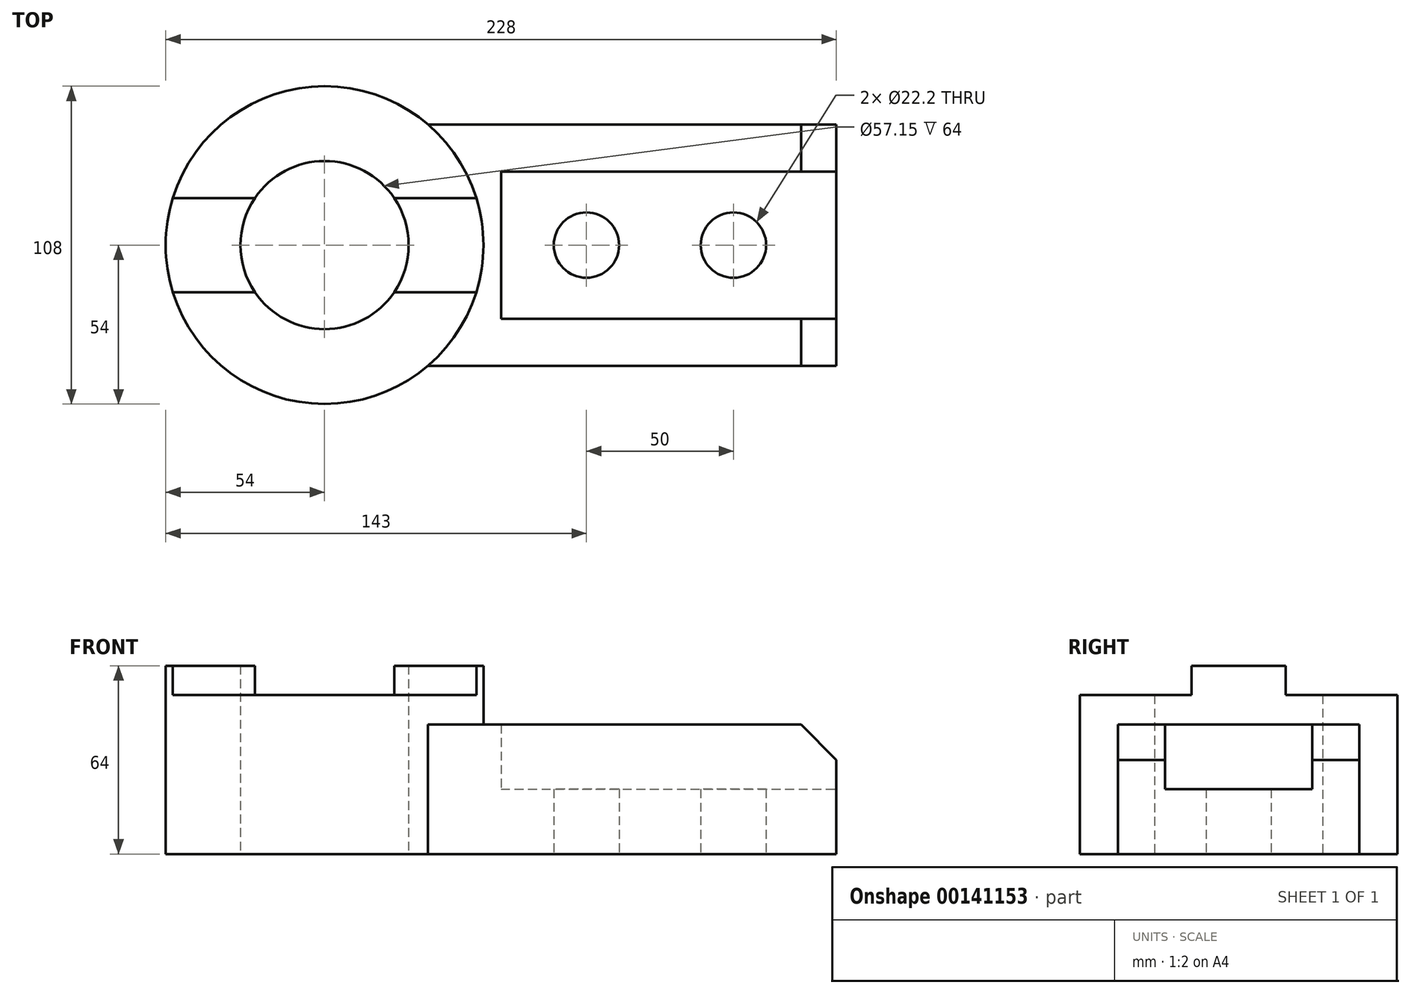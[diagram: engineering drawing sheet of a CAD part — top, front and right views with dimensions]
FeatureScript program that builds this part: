
annotation { "Feature Type Name" : "Feature", "Feature Type Description" : "" }
export const myFeature = defineFeature(function(context is Context, id is Id, definition is map)
    precondition{}
    {
        {
            var Q0;
            Q0=qCreatedBy(makeId("Top.planeOp"),FACE);
            var sketch = newSketch(context, id + "F0", { "sketchPlane" : qUnion([Q0])});
            skCircle(sketch, "E0", {"center": v(0, 0) * mm, "radius": 54 * mm});
            skLineSegment(sketch, "E1", {"start": v(35.14, 41) * mm, "end": v(174, 41) * mm});
            skLineSegment(sketch, "E2", {"start": v(35.14, -41) * mm, "end": v(174, -41) * mm});
            skLineSegment(sketch, "E3", {"start": v(174, -41) * mm, "end": v(174, 41) * mm});
            skCircle(sketch, "E4", {"center": v(0, 0) * mm, "radius": 28.57 * mm});
            skLineSegment(sketch, "E5", {"start": v(174, 25) * mm, "end": v(60, 25) * mm});
            skLineSegment(sketch, "E6", {"start": v(60, 25) * mm, "end": v(60, -25) * mm});
            skLineSegment(sketch, "E7", {"start": v(60, -25) * mm, "end": v(174, -25) * mm});
            skCircle(sketch, "E8", {"center": v(89, 0) * mm, "radius": 11.1 * mm});
            skCircle(sketch, "E9", {"center": v(139, 0) * mm, "radius": 11.1 * mm});
            skLineSegment(sketch, "E10", {"start": v(-51.58, 16) * mm, "end": v(-23.68, 16) * mm});
            skLineSegment(sketch, "E11", {"start": v(23.68, 16) * mm, "end": v(51.58, 16) * mm});
            skLineSegment(sketch, "E12", {"start": v(-51.58, -16) * mm, "end": v(-23.68, -16) * mm});
            skLineSegment(sketch, "E13", {"start": v(23.68, -16) * mm, "end": v(51.58, -16) * mm});
            skSolve(sketch);
        }
        {
            var Q0;
            {var subQ0=sQuery(id+"F0.wireOp",EDGE,"E1");Q0=makeQuery(id+"F0.imprint","IMPRINT",FACE,{"disambiguationData":[TD([[makeQuery(id+"F0.imprint","IMPRINT",EDGE,{"derivedFrom":subQ0}),-1.0]])]});}
            extrude(context, id + "F1", {"entities" : qUnion([Q0]), "depth" : 44 * mm});
        }
        {
            var Q0;
            {var subQ1=sQuery(id+"F0.wireOp",EDGE,"E5");Q0=makeQuery(id+"F0.imprint","IMPRINT",FACE,{"disambiguationData":[TD([[makeQuery(id+"F0.imprint","IMPRINT",EDGE,{"derivedFrom":subQ1}),1.0]])]});}
            extrude(context, id + "F2", {"entities" : qUnion([Q0]), "operationType" : NewBodyOperationType.ADD, "depth" : 22 * mm});
        }
        {
            var Q0;
            {var subQ0=sQuery(id+"F0.wireOp",EDGE,"E12");Q0=makeQuery(id+"F0.imprint","IMPRINT",FACE,{"disambiguationData":[TD([[makeQuery(id+"F0.imprint","IMPRINT",EDGE,{"derivedFrom":subQ0}),-1.0]])]});}
            var Q1;
            {var subQ0=sQuery(id+"F0.wireOp",EDGE,"E10");Q1=makeQuery(id+"F0.imprint","IMPRINT",FACE,{"disambiguationData":[TD([[makeQuery(id+"F0.imprint","IMPRINT",EDGE,{"derivedFrom":subQ0}),1.0]])]});}
            extrude(context, id + "F3", {"entities" : qUnion([Q0, Q1]), "operationType" : NewBodyOperationType.ADD, "depth" : 54 * mm});
        }
        {
            var Q0;
            {var subQ0=sQuery(id+"F0.wireOp",EDGE,"E10");Q0=makeQuery(id+"F0.imprint","IMPRINT",FACE,{"disambiguationData":[TD([[makeQuery(id+"F0.imprint","IMPRINT",EDGE,{"derivedFrom":subQ0}),-1.0]])]});}
            var Q1;
            {var subQ0=sQuery(id+"F0.wireOp",EDGE,"E11");Q1=makeQuery(id+"F0.imprint","IMPRINT",FACE,{"disambiguationData":[TD([[makeQuery(id+"F0.imprint","IMPRINT",EDGE,{"derivedFrom":subQ0}),-1.0]])]});}
            var Q2;
            Q2 = qSketchRegion(id + "F5", true);
            extrude(context, id + "F4", {"entities" : qUnion([Q0, Q1, Q2]), "operationType" : NewBodyOperationType.ADD, "depth" : 64 * mm});
        }
        {
            var Q0;
            Q0=makeQuery(id+"F1.opExtrude","SWEPT_FACE",FACE,{"disambiguationData":[OSD([sQuery(id+"F0.wireOp",EDGE,"E2")])]});
            var sketch = newSketch(context, id + "F5", { "sketchPlane" : qUnion([Q0])});
            skLineSegment(sketch, "E14", {"start": v(162, 44) * mm, "end": v(174, 32) * mm});
            skLineSegment(sketch, "E15", {"start": v(174, 32) * mm, "end": v(174, 44) * mm});
            skLineSegment(sketch, "E16", {"start": v(174, 44) * mm, "end": v(162, 44) * mm});
            skSolve(sketch);
        }
        {
            var Q0;
            Q0 = qSketchRegion(id + "F5", true);
            extrude(context, id + "F6", {"entities" : qUnion([Q0]), "operationType" : NewBodyOperationType.REMOVE, "endBound" : BoundingType.THROUGH_ALL, "oppositeDirection" : true, "depth" : 25 * mm});
        }
    });
